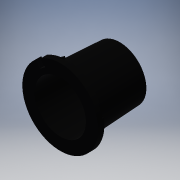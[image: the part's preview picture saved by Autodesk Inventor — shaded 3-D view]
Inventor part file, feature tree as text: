
AUTODESK INVENTOR PART (.ipt)
format: ipt  version: 2016 (Build 200138000, 138)  size: 278,016 bytes
history: native  units: mm
features: sketch x13, extrude x8, plane x3, loft x3, projected_geometry x3
ambient origin geometry x8: Origin, YZ Plane, XZ Plane, XY Plane, X Axis, Y Axis, Z Axis, Center Point
bodies: Solid1 (feature_tree)
feature tree (30):
  extrude  "Extrusion1"  Depth=19.05mm TaperAngle=0.0deg
  plane  "Work Plane1"
  loft  "Loft1"
  loft  "Loft2"
  extrude  "Extrusion2"  TaperAngle=0.0deg  [1 undecoded]
  extrude  "Extrusion3"  Depth=9.0mm
  plane  "Work Plane2"
  plane  "Work Plane3"
  sketch  "Sketch11"  dims[d20=12.0mm d21=20.0mm]
  loft  "Loft3"
  extrude  "Extrusion4"  Depth=35.0mm
  extrude  "Extrusion5"  Depth=20.0mm
  extrude  "Extrusion6"  Depth=4.0mm TaperAngle=0.0deg
  extrude  "Extrusion7"  Depth=23.0mm
  extrude  "Extrusion8"  [1 undecoded]
  sketch  "Sketch2"  dims[d1=239.7125mm d2=19.05mm d3=0.0mm]
  sketch  "Sketch3"  dims[d4=168.275mm d5=168.275mm]
  sketch  "Sketch5"  dims[d6=9.0mm d7=27.0mm]
  sketch  "Sketch6"  dims[d8=9.0mm d9=0.0mm d10=90.0deg]
  sketch  "Sketch7"  dims[d11=0.0mm d12=90.0deg d13=9.0mm]
  sketch  "Sketch8"  dims[d14=161.925mm d15=0.0mm d16=90.0deg]
  sketch  "Sketch9"  dims[d17=0.0mm d18=90.0deg d19=35.0mm]
  projected_geometry  "Projected Loop1"
  sketch  "Sketch12"  dims[d22=50.0mm d24=360.0deg d26=4.0mm d27=0.0mm]
  sketch  "Sketch13"  dims[d28=22.0mm d29=23.0mm]
  sketch  "Sketch14"  dims[d30=4.0mm d31=0.0mm d32=-5.0mm d33=-10.0mm]
  sketch  "Sketch15"  dims[d39=22.0mm]
  sketch  "Sketch16"  dims[d40=0.0mm d41=90.0deg d42=0.0mm d43=90.0deg d44=11.0mm d45=0.0mm d46=60.0mm d48=360.0deg d50=30.0mm d51=4.0mm d52=0.0mm d53=60.0mm d55=360.0deg d58=4.0mm d59=0.0mm d60=62.0mm d61=5.0mm d62=0.0mm d63=16.0mm d64=10.0mm d65=22.5mm d66=10.0mm d67=20.0mm d68=0.0mm]
  projected_geometry  "Project Cut Edges1"
  projected_geometry  "Project Cut Edges2"
note: 2 required parameter values undecoded (feature->parameter linkage not recoverable at this tier; creation-order binding heuristic only, values carry confidence <= 0.55)
